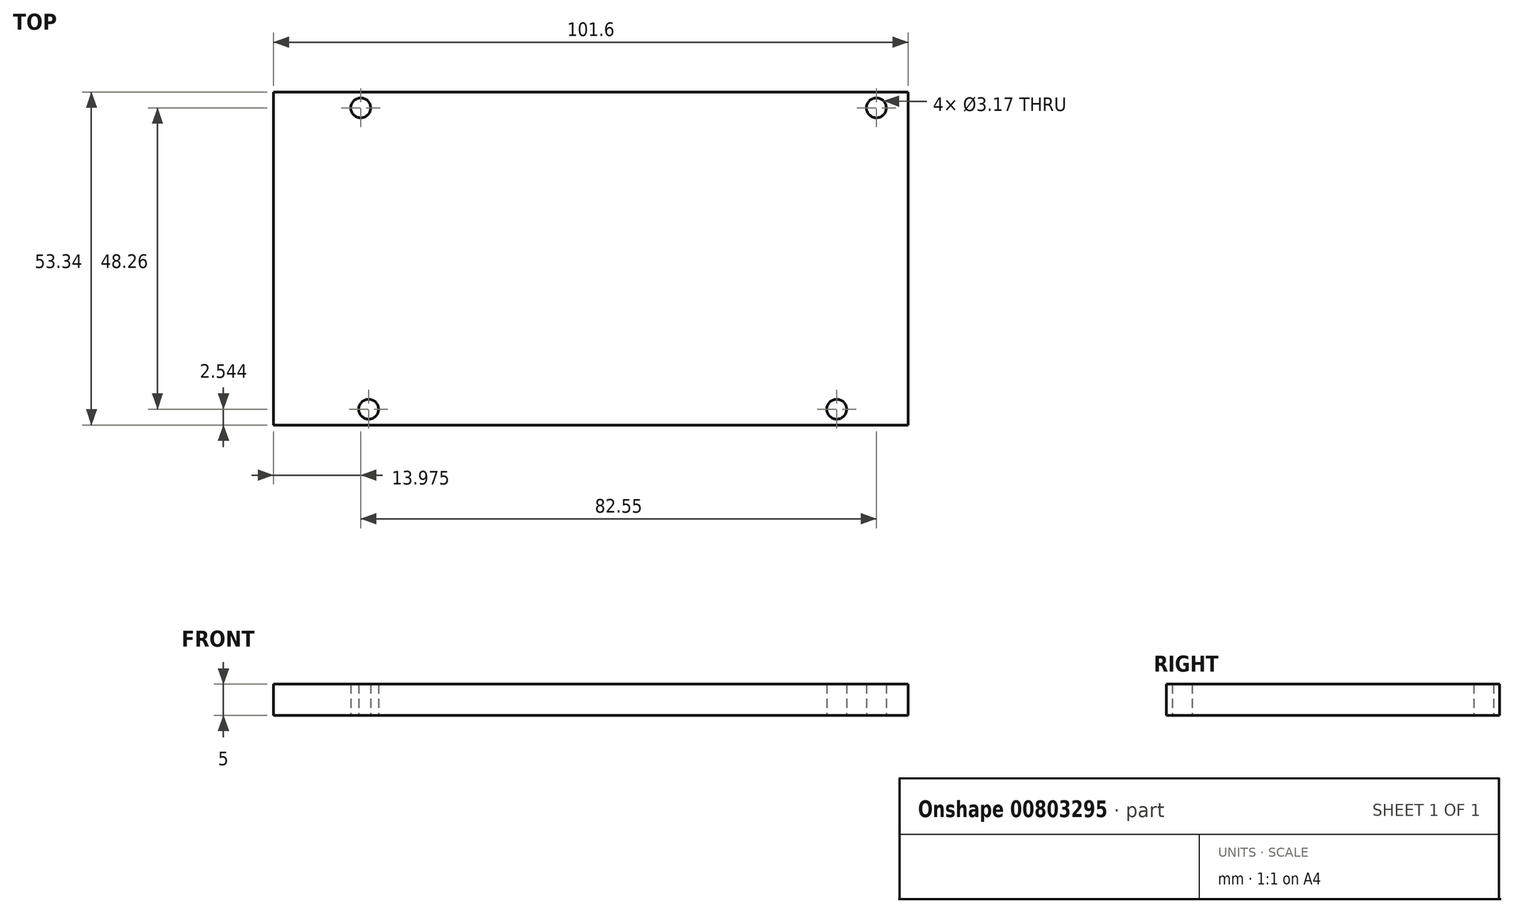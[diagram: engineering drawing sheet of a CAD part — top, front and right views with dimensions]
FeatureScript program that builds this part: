
annotation { "Feature Type Name" : "Feature", "Feature Type Description" : "" }
export const myFeature = defineFeature(function(context is Context, id is Id, definition is map)
    precondition{}
    {
        {
            var Q0;
            Q0=qCreatedBy(makeId("Top.planeOp"),FACE);
            var sketch = newSketch(context, id + "F0", { "sketchPlane" : qUnion([Q0])});
            skLineSegment(sketch, "E0.bottom", {"start": v(-53.36, -24.4) * mm, "end": v(48.24, -24.4) * mm});
            skLineSegment(sketch, "E0.top", {"start": v(-53.36, 28.93) * mm, "end": v(48.24, 28.93) * mm});
            skLineSegment(sketch, "E0.left", {"start": v(-53.36, -24.4) * mm, "end": v(-53.36, 28.93) * mm});
            skLineSegment(sketch, "E0.right", {"start": v(48.24, -24.4) * mm, "end": v(48.24, 28.93) * mm});
            skCircle(sketch, "E1", {"center": v(-38.12, -21.87) * mm, "radius": 1.59 * mm});
            skCircle(sketch, "E2", {"center": v(36.81, -21.87) * mm, "radius": 1.59 * mm});
            skCircle(sketch, "E3", {"center": v(43.16, 26.4) * mm, "radius": 1.59 * mm});
            skCircle(sketch, "E4", {"center": v(-39.39, 26.4) * mm, "radius": 1.59 * mm});
            skSolve(sketch);
        }
        {
            var Q0;
            Q0=makeQuery(id+"F0.imprint","IMPRINT",FACE,{"disambiguationData":[TD([[makeQuery(id+"F0.imprint","IMPRINT",EDGE,{"derivedFrom":sQuery(id+"F0.wireOp",EDGE,"E0.bottom")}),1.0]])]});
            extrude(context, id + "F1", {"entities" : qUnion([Q0]), "depth" : 5 * mm, "offsetDistance" : 25 * mm});
        }
    });
